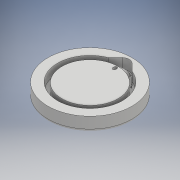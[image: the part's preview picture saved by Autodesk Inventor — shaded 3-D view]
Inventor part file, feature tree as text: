
AUTODESK INVENTOR PART (.ipt)
format: ipt  version: 2018.3 (Build 223284000, 284)  size: 364,032 bytes
history: native  units: mm
features: sketch x6, extrude x5, plane x5, projected_geometry x4, fillet x3, revolve x2, other x1
ambient origin geometry x8: Origin, YZ Plane, XZ Plane, XY Plane, X Axis, Y Axis, Z Axis, Center Point
bodies: Solid1 (feature_tree)
feature tree (26):
  extrude  "Extrusion1"  Depth=25.0mm TaperAngle=0.0deg
  extrude  "Extrusion2"  Depth=20.0mm TaperAngle=0.0deg
  extrude  "Extrusion4"  Depth=17.5mm
  fillet  "Fillet1"  [1 undecoded]
  plane  "Work Plane1"
  other  "Work Axis1"
  plane  "Work Plane9"
  plane  "Work Plane10"
  extrude  "Extrusion10"  Depth=5.0mm
  revolve  "Revolution3"  Angle=90.0deg
  fillet  "Fillet3"  [1 undecoded]
  extrude  "Extrusion13"  Depth=1.0mm TaperAngle=0.0deg
  fillet  "Fillet5"  [1 undecoded]
  revolve  "Revolution5"  [1 undecoded]
  sketch  "Sketch1"  dims[d0=150.0mm d1=25.0mm d2=0.0mm]
  sketch  "Sketch2"  dims[d4=116.0mm d5=20.0mm d6=0.0mm]
  sketch  "Sketch3"  dims[d12=25.0mm d13=17.5mm d15=45.0deg]
  plane  "Work Plane2"
  plane  "Work Plane3"
  sketch  "Sketch13"  dims[d16=5.0mm d17=0.0mm d24=5.0mm]
  sketch  "Sketch16"  dims[d25=0.0mm d29=90.0deg d30=90.0deg]
  projected_geometry  "Projected Loop8"
  projected_geometry  "Projected Loop9"
  sketch  "Sketch18"  dims[d60=8.0mm d61=20.0mm d62=0.0mm d69=180.0deg d70=10.0mm d72=58.0mm d74=4.0mm d76=5.75mm d77=10.0mm d78=17.0mm d79=0.0mm d80=17.0mm d81=1.0mm d82=90.0deg]
  projected_geometry  "Projected Loop10"
  projected_geometry  "Projected Loop11"
note: 4 required parameter values undecoded (feature->parameter linkage not recoverable at this tier; creation-order binding heuristic only, values carry confidence <= 0.55)